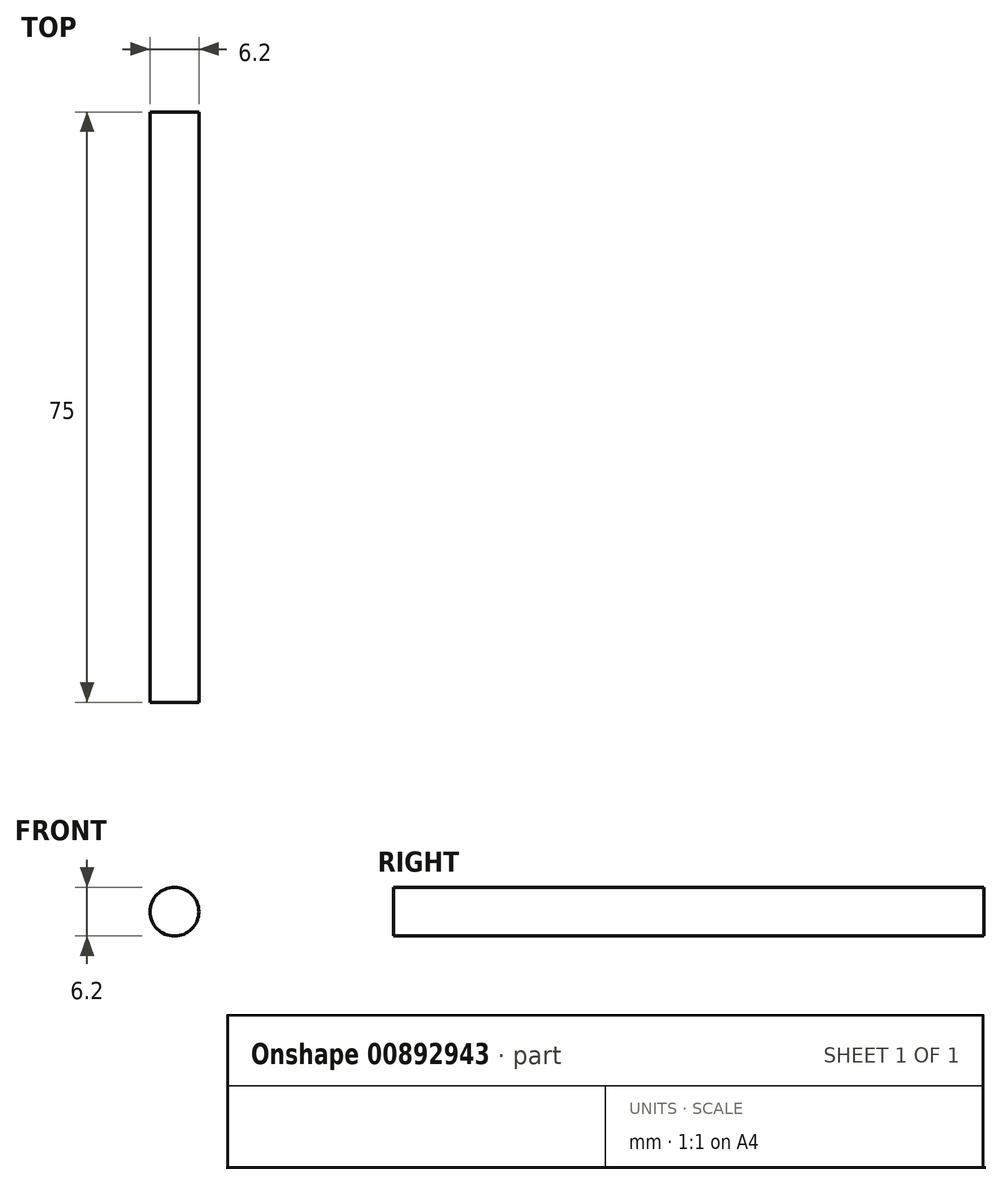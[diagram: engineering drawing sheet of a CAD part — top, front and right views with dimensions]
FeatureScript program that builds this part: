
annotation { "Feature Type Name" : "Feature", "Feature Type Description" : "" }
export const myFeature = defineFeature(function(context is Context, id is Id, definition is map)
    precondition{}
    {
        {
            var Q0;
            Q0=qCreatedBy(makeId("Front.planeOp"),FACE);
            var sketch = newSketch(context, id + "F0", { "sketchPlane" : qUnion([Q0])});
            skCircle(sketch, "E0", {"center": v(0, 0) * mm, "radius": 3.1 * mm});
            skSolve(sketch);
        }
        {
            var Q0;
            Q0 = qSketchRegion(id + "F0", true);
            extrude(context, id + "F1", {"entities" : qUnion([Q0]), "depth" : (75 / 2) * mm, "offsetDistance" : 25 * mm, "hasSecondDirection" : true, "secondDirectionOppositeDirection" : true, "secondDirectionDepth" : 37.5 * mm});
        }
    });
